# Revit family: 265-91-001 DN80-150
name_source: partatom
category: Pipe Accessories
units: mm (PartAtom-declared; Revit-internal decimal feet)

## family parameters
Always vertical = Yes
Cut with Voids When Loaded = No
Part Type = Valve - Breaks Into
Round Connector Dimension = Use Diameter
Shared = No
Work Plane-Based = No

## types (4) — shared parameters
25 = 25 mm  [stored 0.082021 ft]
Bolt.no = 8 mm  [stored 0.0262467 ft]
DN080_PN16 = 265-9-0080-10-14036400
DN100_PN16 = 265-9-0100-10-14036400
DN125_PN16 = 265-9-0125-10-14036400
DN150_PN16 = 265-9-0150-10-14036400
Description_ = AVK DISMANTLING JOINT WITH CENTRE FLANGE, PN10/16
FL_T = 19 mm  [stored 0.062336 ft]
FL_T/2 = 10 mm  [stored 0.0328084 ft]
L1 = 136 mm
L11 = 200 mm  [stored 0.656168 ft]
L3 = 10 mm  [stored 0.0328084 ft]
Nut_T = 14 mm  [stored 0.0459318 ft]
PN = 16 mm  [stored 0.0524934 ft]
Raised_dis = 3 mm  [stored 0.00984252 ft]
Search_table = 265-91-001 DN80-150
T = 6 mm  [stored 0.019685 ft]
T1 = 14 mm  [stored 0.0459318 ft]
URL_product_pages = https://www.avkvalves.com
zero-valued in all types: Default Elevation

## per-type parameters (varying)
| type | B1 | Bore | D | DN | L | L2 | PCD | S | S11 | offset | raised_R |
| DN080_PN16 | 26 mm | 40 mm  [stored 0.131234 ft] | 100 mm  [stored 0.328084 ft] | 80 mm  [stored 0.262467 ft] | 325 mm  [stored 1.06627 ft] | 21 mm | 80 mm  [stored 0.262467 ft] | 16 mm  [stored 0.0524934 ft] | 22 mm | 6 mm  [stored 0.019685 ft] | 75 mm |
| DN100_PN16 | 26 mm | 50 mm  [stored 0.164042 ft] | 110 mm  [stored 0.360892 ft] | 100 mm  [stored 0.328084 ft] | 325 mm  [stored 1.06627 ft] | 21 mm | 90 mm  [stored 0.295276 ft] | 16 mm  [stored 0.0524934 ft] | 22 mm | 6 mm  [stored 0.019685 ft] | 83 mm |
| DN125_PN16 | 26 mm | 63 mm | 125 mm  [stored 0.410105 ft] | 125 mm  [stored 0.410105 ft] | 325 mm  [stored 1.06627 ft] | 21 mm | 105 mm  [stored 0.344488 ft] | 16 mm  [stored 0.0524934 ft] | 22 mm | 6 mm  [stored 0.019685 ft] | 94 mm |
| DN150_PN16 | 27 mm  [stored 0.0885827 ft] | 75 mm | 143 mm | 150 mm  [stored 0.492126 ft] | 340 mm  [stored 1.11549 ft] | 22 mm | 120 mm  [stored 0.393701 ft] | 20 mm  [stored 0.0656168 ft] | 27 mm  [stored 0.0885827 ft] | 7 mm  [stored 0.0229659 ft] | 107 mm |

note: [stored X ft] marks values corroborated as IEEE doubles in the binary element streams (Revit-internal decimal feet)

## geometry (parser evidence)
native form markers: Sweep x6
no freeform markers — native parametric forms only
